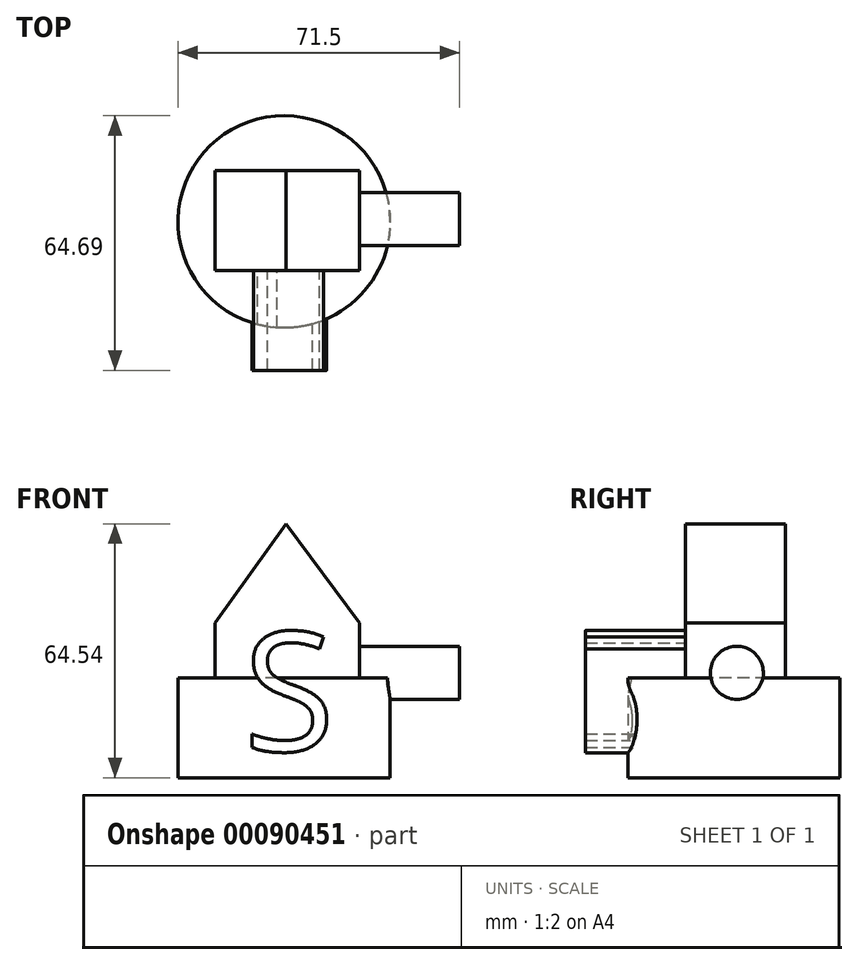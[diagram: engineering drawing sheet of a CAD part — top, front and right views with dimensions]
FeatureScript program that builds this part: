
annotation { "Feature Type Name" : "Feature", "Feature Type Description" : "" }
export const myFeature = defineFeature(function(context is Context, id is Id, definition is map)
    precondition{}
    {
        {
            var Q0;
            Q0=qCreatedBy(makeId("Front.planeOp"),FACE);
            var sketch = newSketch(context, id + "F0", { "sketchPlane" : qUnion([Q0])});
            skLineSegment(sketch, "E0.bottom", {"start": v(0, 39.37) * mm, "end": v(36.71, 39.37) * mm});
            skLineSegment(sketch, "E0.top", {"start": v(0, 0) * mm, "end": v(36.71, 0) * mm});
            skLineSegment(sketch, "E0.left", {"start": v(0, 39.37) * mm, "end": v(0, 0) * mm});
            skLineSegment(sketch, "E0.right", {"start": v(36.71, 39.37) * mm, "end": v(36.71, 0) * mm});
            skLineSegment(sketch, "E1", {"start": v(0, 39.37) * mm, "end": v(18.01, 64.54) * mm});
            skLineSegment(sketch, "E2", {"start": v(18.01, 64.54) * mm, "end": v(36.71, 39.37) * mm});
            skSolve(sketch);
        }
        {
            var Q0;
            Q0 = qSketchRegion(id + "F0", true);
            extrude(context, id + "F1", {"entities" : qUnion([Q0]), "depth" : 25.4 * mm});
        }
        {
            var Q0;
            Q0=makeQuery(id+"F1.opExtrude","CAP_FACE",FACE,{"disambiguationData":[OSD([sQuery(id+"F0.wireOp",EDGE,"E0.top"),sQuery(id+"F0.wireOp",EDGE,"E0.left"),sQuery(id+"F0.wireOp",EDGE,"E0.right"),sQuery(id+"F0.wireOp",EDGE,"E1"),sQuery(id+"F0.wireOp",EDGE,"E2")])],"isStart":false});
            var sketch = newSketch(context, id + "F2", { "sketchPlane" : qUnion([Q0])});
            skText(sketch, "E3", { "text": "S", "fontName": "OpenSans-Regular.ttf"});
            const initialGuessF2  = {"E3": [0.00716, 0.00681, 1, 0, 0.03048]};
            skSetInitialGuess(sketch, initialGuessF2);
            skSolve(sketch);
        }
        {
            var Q0;
            Q0 = qSketchRegion(id + "F2", true);
            extrude(context, id + "F3", {"entities" : qUnion([Q0]), "operationType" : NewBodyOperationType.ADD, "depth" : 25.4 * mm});
        }
        {
            var Q0;
            Q0=makeQuery(id+"F1.opExtrude","SWEPT_FACE",FACE,{"disambiguationData":[OSD([sQuery(id+"F0.wireOp",EDGE,"E0.right")])]});
            var sketch = newSketch(context, id + "F4", { "sketchPlane" : qUnion([Q0])});
            skCircle(sketch, "E4", {"center": v(-12.35, 26.67) * mm, "radius": 6.74 * mm});
            skSolve(sketch);
        }
        {
            var Q0;
            Q0=makeQuery(id+"F1.opExtrude","SWEPT_FACE",FACE,{"disambiguationData":[OSD([sQuery(id+"F0.wireOp",EDGE,"E1")])]});
            extrude(context, id + "F5", {"entities" : qUnion([Q0]), "operationType" : NewBodyOperationType.REMOVE, "depth" : 25.4 * mm});
        }
        {
            var Q0;
            Q0=makeQuery(id+"F4.imprint","IMPRINT",FACE,{"disambiguationData":[TD([[makeQuery(id+"F4.imprint","IMPRINT",EDGE,{"derivedFrom":sQuery(id+"F4.wireOp",EDGE,"E4")}),1.0]])]});
            extrude(context, id + "F6", {"entities" : qUnion([Q0]), "operationType" : NewBodyOperationType.ADD, "depth" : 25.4 * mm});
        }
        {
            var Q0;
            Q0=qCreatedBy(makeId("Top.planeOp"),FACE);
            var sketch = newSketch(context, id + "F7", { "sketchPlane" : qUnion([Q0])});
            skCircle(sketch, "E5", {"center": v(17.55, -13.05) * mm, "radius": 26.94 * mm});
            skSolve(sketch);
        }
        {
            var Q0;
            Q0=makeQuery(id+"F7.imprint","IMPRINT",FACE,{"disambiguationData":[TD([[makeQuery(id+"F7.imprint","IMPRINT",EDGE,{"derivedFrom":sQuery(id+"F7.wireOp",EDGE,"E5")}),1.0]])]});
            extrude(context, id + "F8", {"entities" : qUnion([Q0]), "operationType" : NewBodyOperationType.ADD, "depth" : 25.4 * mm});
        }
    });
